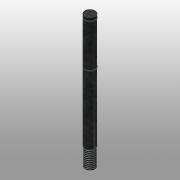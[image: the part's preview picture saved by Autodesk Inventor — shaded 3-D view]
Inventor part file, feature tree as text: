
AUTODESK INVENTOR PART (.ipt)
format: ipt  version: 2015 (Build 190159000, 159)  size: 96,768 bytes
history: native  units: mm
features: other x3, sketch x1
ambient origin geometry x8: Origin, YZ Plane, XZ Plane, XY Plane, X Axis, Y Axis, Z Axis, Center Point
bodies: Solid1 (feature_tree)
feature tree (4):
  other  "500-104.ipt"
  other  "Solid1::500-104.ipt"
  other  "TaggingFeature1"
  sketch  "Sketch1"  dims[d0=10.0mm]
